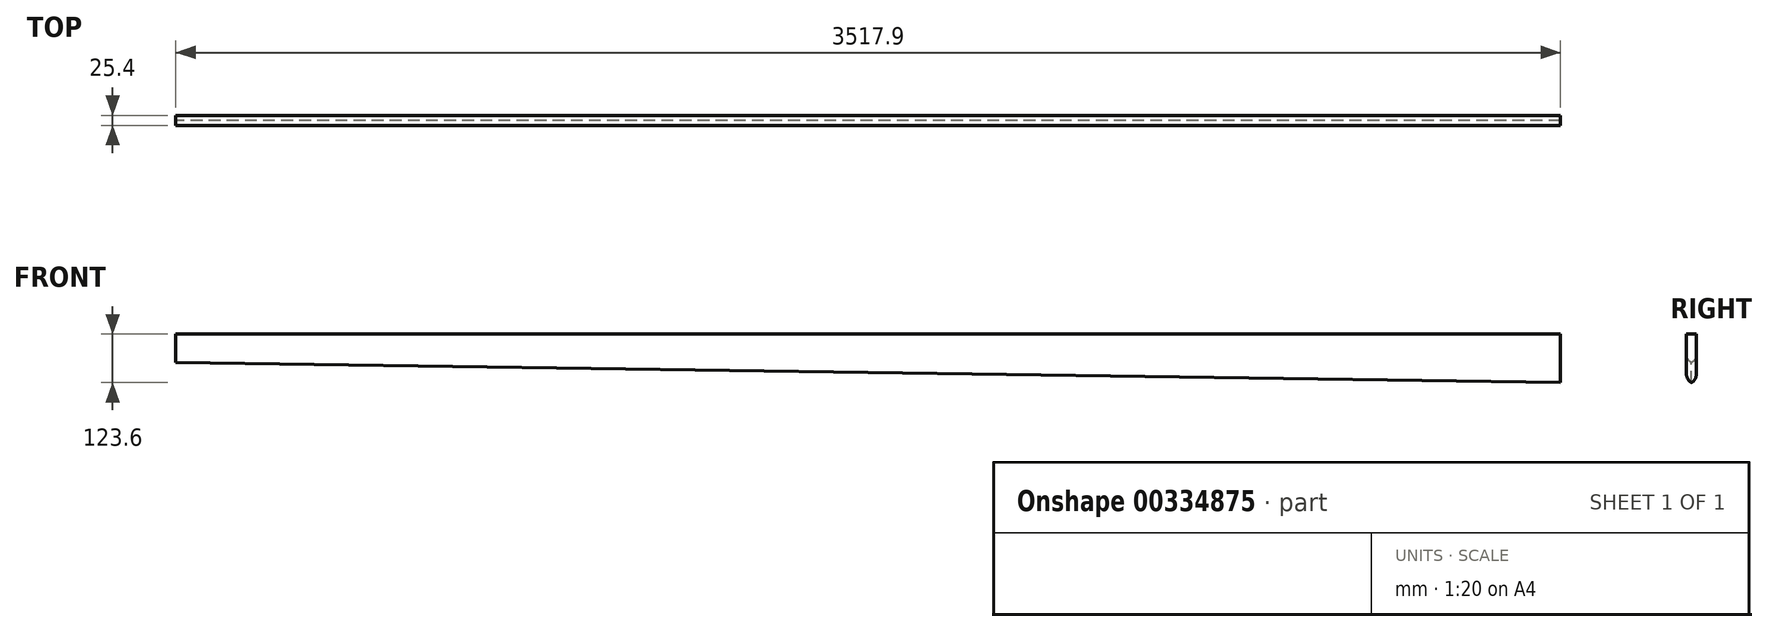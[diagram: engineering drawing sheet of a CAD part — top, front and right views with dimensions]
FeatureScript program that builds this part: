
annotation { "Feature Type Name" : "Feature", "Feature Type Description" : "" }
export const myFeature = defineFeature(function(context is Context, id is Id, definition is map)
    precondition{}
    {
        {
            var Q0;
            Q0=qCreatedBy(makeId("Front.planeOp"),FACE);
            var sketch = newSketch(context, id + "F0", { "sketchPlane" : qUnion([Q0])});
            skLineSegment(sketch, "E0", {"start": v(0, 0) * mm, "end": v(3517.9, 0) * mm});
            skLineSegment(sketch, "E1", {"start": v(3517.9, 0) * mm, "end": v(3517.9, -127) * mm});
            skLineSegment(sketch, "E2", {"start": v(3517.9, -127) * mm, "end": v(0, -76.2) * mm});
            skLineSegment(sketch, "E3", {"start": v(0, -76.2) * mm, "end": v(0, 0) * mm});
            skSolve(sketch);
        }
        {
            var Q0;
            Q0=makeQuery(id+"F0.imprint","IMPRINT",FACE,{"disambiguationData":[TD([[makeQuery(id+"F0.imprint","IMPRINT",EDGE,{"derivedFrom":sQuery(id+"F0.wireOp",EDGE,"E0")}),-1.0]])]});
            extrude(context, id + "F1", {"entities" : qUnion([Q0]), "depth" : 25.4 * mm});
        }
        {
            var Q0;
            Q0=makeQuery(id+"F1.opExtrude","CAP_EDGE",EDGE,{"disambiguationData":[OSD([sQuery(id+"F0.wireOp",EDGE,"E2")])],"isStart":false});
            var Q1;
            Q1=makeQuery(id+"F1.opExtrude","CAP_EDGE",EDGE,{"disambiguationData":[OSD([sQuery(id+"F0.wireOp",EDGE,"E2")])],"isStart":true});
            fillet(context, id + "F2", {"entities" : qUnion([Q0, Q1]), "radius" : 25.4 * mm, "tangentPropagation" : true, "allowEdgeOverflow" : false});
        }
    });
